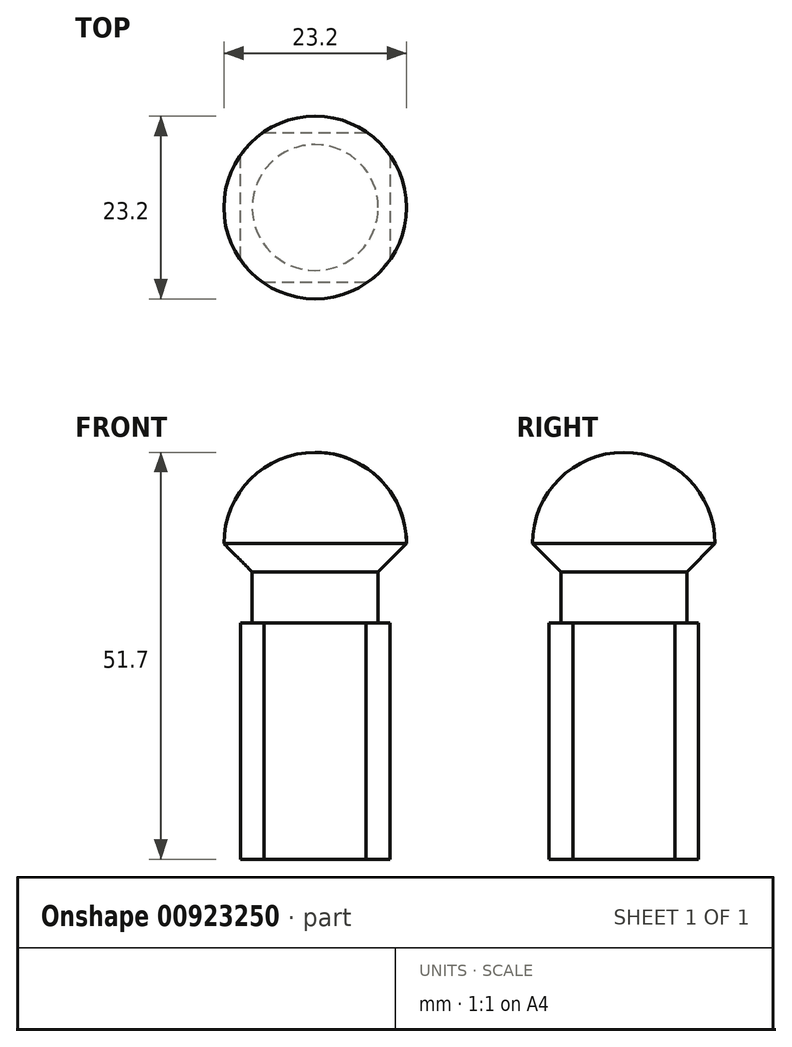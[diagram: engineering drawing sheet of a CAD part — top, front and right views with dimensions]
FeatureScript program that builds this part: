
annotation { "Feature Type Name" : "Feature", "Feature Type Description" : "" }
export const myFeature = defineFeature(function(context is Context, id is Id, definition is map)
    precondition{}
    {
        {
            var Q0;
            Q0=qCreatedBy(makeId("Front.planeOp"),FACE);
            var sketch = newSketch(context, id + "F0", { "sketchPlane" : qUnion([Q0])});
            skLineSegment(sketch, "E0", {"start": v(8, 0) * mm, "end": v(8, 6.5) * mm});
            skLineSegment(sketch, "E1", {"start": v(0, 0) * mm, "end": v(0, 21.7) * mm});
            skArc(sketch, "E2.trimOffspring", {"start": v(11.6, 10.1) * mm, "mid": v(8.2, 18.3) * mm, "end": v(0, 21.7) * mm});
            skLineSegment(sketch, "E3", {"start": v(8, 6.5) * mm, "end": v(11.6, 10.1) * mm});
            skPoint(sketch, "E4.end.orphan", {"position": v(8, 10.1) * mm});
            skLineSegment(sketch, "E5", {"start": v(0, 0) * mm, "end": v(0, -30) * mm});
            skLineSegment(sketch, "E6", {"start": v(0, -30) * mm, "end": v(11.5, -30) * mm});
            skLineSegment(sketch, "E7", {"start": v(11.5, -30) * mm, "end": v(11.5, 0) * mm});
            skLineSegment(sketch, "E8", {"start": v(11.5, 0) * mm, "end": v(8, 0) * mm});
            skSolve(sketch);
        }
        {
            var Q0;
            Q0=makeQuery(id+"F0.imprint","IMPRINT",FACE,{"disambiguationData":[TD([[makeQuery(id+"F0.imprint","IMPRINT",EDGE,{"derivedFrom":sQuery(id+"F0.wireOp",EDGE,"E0")}),1.0]])]});
            var Q1;
            Q1=sQuery(id+"F0.wireOp",EDGE,"E1");
            revolve(context, id + "F1", {"surfaceOperationType" : NewSurfaceOperationType.NEW, "entities" : qUnion([Q0]), "axis" : qUnion([Q1]), "revolveType" : RevolveType.FULL});
        }
        {
            var Q0;
            Q0=makeQuery(id+"F1.opRevolve","SWEPT_FACE",FACE,{"disambiguationData":[OSD([sQuery(id+"F0.wireOp",EDGE,"E6")])]});
            var sketch = newSketch(context, id + "F2", { "sketchPlane" : qUnion([Q0])});
            skLineSegment(sketch, "E9", {"start": v(9.5, 0) * mm, "end": v(9.5, 6.48) * mm});
            skLineSegment(sketch, "E10", {"start": v(6.48, 9.5) * mm, "end": v(-6.48, 9.5) * mm});
            skLineSegment(sketch, "E11", {"start": v(-9.5, 6.48) * mm, "end": v(-9.5, -6.48) * mm});
            skLineSegment(sketch, "E12", {"start": v(-6.48, -9.5) * mm, "end": v(6.48, -9.5) * mm});
            skLineSegment(sketch, "E13", {"start": v(9.5, -6.48) * mm, "end": v(9.5, 0) * mm});
            skPoint(sketch, "E14.endSnap0", {"position": v(-9.5, 0) * mm});
            skPoint(sketch, "E15.orphan", {"position": v(0, 0) * mm});
            skCircle(sketch, "E16", {"center": v(0, 0) * mm, "radius": 11.5 * mm});
            skPoint(sketch, "E17.orphan", {"position": v(-9.5, 9.5) * mm});
            skPoint(sketch, "E18.orphan", {"position": v(-9.5, -9.5) * mm});
            skPoint(sketch, "E19.orphan", {"position": v(9.5, -9.5) * mm});
            skSolve(sketch);
        }
        {
            var Q0;
            {var subQ0=sQuery(id+"F2.wireOp",EDGE,"E10");Q0=makeQuery(id+"F2.imprint","IMPRINT",FACE,{"disambiguationData":[TD([[makeQuery(id+"F2.imprint","IMPRINT",EDGE,{"derivedFrom":subQ0}),-1.0]])]});}
            var Q1;
            {var subQ0=sQuery(id+"F2.wireOp",EDGE,"E9");Q1=makeQuery(id+"F2.imprint","IMPRINT",FACE,{"disambiguationData":[TD([[makeQuery(id+"F2.imprint","IMPRINT",EDGE,{"derivedFrom":subQ0}),-1.0]])]});}
            var Q2;
            {var subQ0=sQuery(id+"F2.wireOp",EDGE,"E11");Q2=makeQuery(id+"F2.imprint","IMPRINT",FACE,{"disambiguationData":[TD([[makeQuery(id+"F2.imprint","IMPRINT",EDGE,{"derivedFrom":subQ0}),-1.0]])]});}
            var Q3;
            {var subQ0=sQuery(id+"F2.wireOp",EDGE,"E12");Q3=makeQuery(id+"F2.imprint","IMPRINT",FACE,{"disambiguationData":[TD([[makeQuery(id+"F2.imprint","IMPRINT",EDGE,{"derivedFrom":subQ0}),-1.0]])]});}
            extrude(context, id + "F3", {"entities" : qUnion([Q0, Q1, Q2, Q3]), "operationType" : NewBodyOperationType.REMOVE, "oppositeDirection" : true, "depth" : 30 * mm, "offsetDistance" : 25 * mm});
        }
    });
